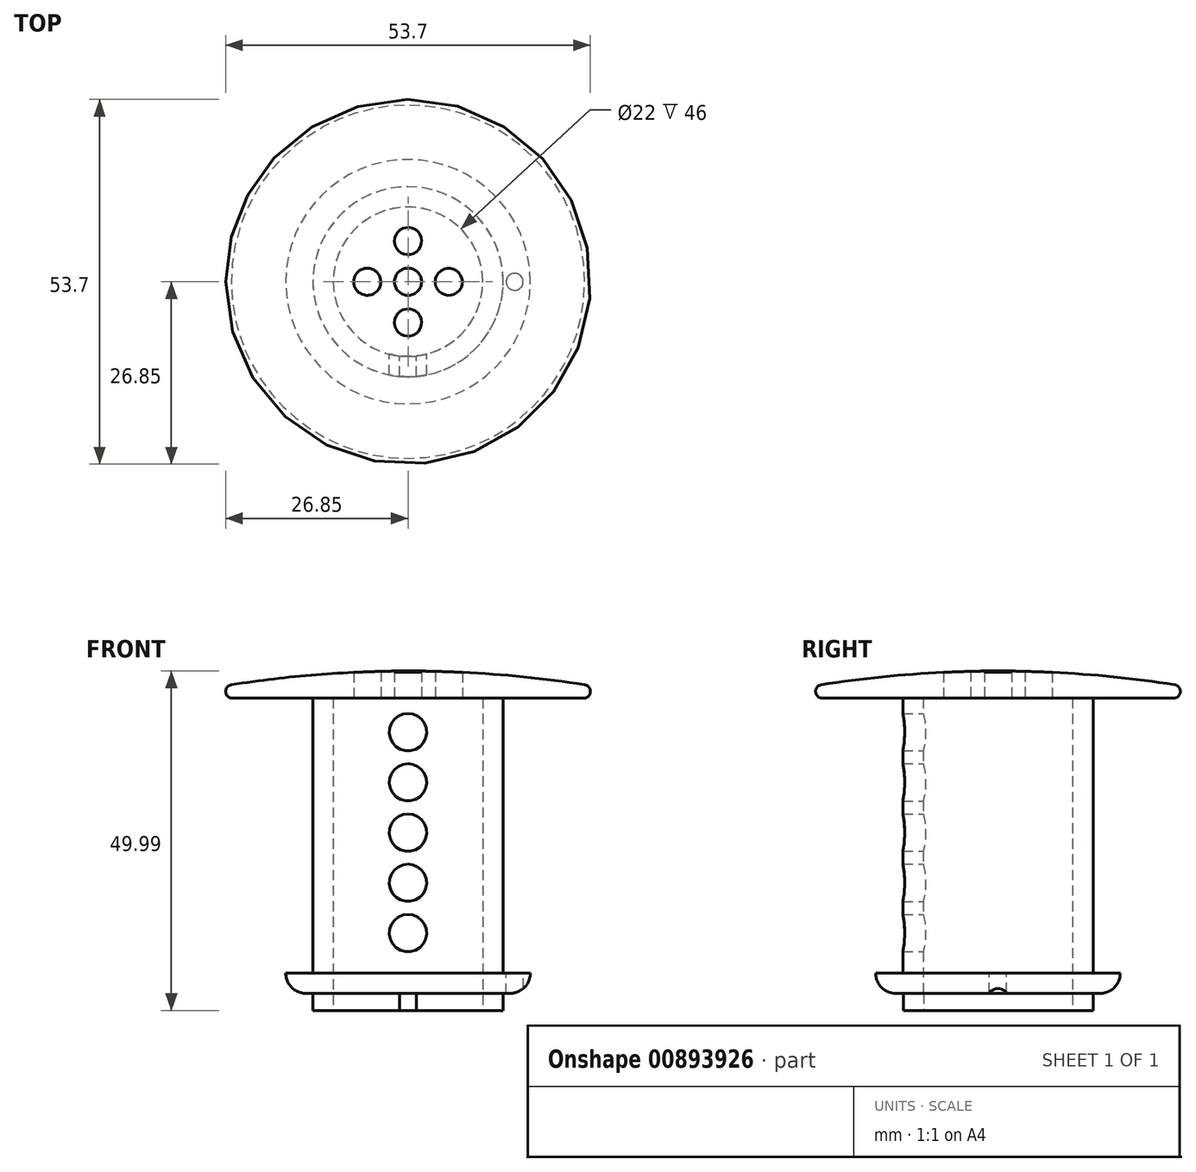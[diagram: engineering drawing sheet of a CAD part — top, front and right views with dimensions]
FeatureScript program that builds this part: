
annotation { "Feature Type Name" : "Feature", "Feature Type Description" : "" }
export const myFeature = defineFeature(function(context is Context, id is Id, definition is map)
    precondition{}
    {
        {
            var Q0;
            Q0=qCreatedBy(makeId("Front.planeOp"),FACE);
            var sketch = newSketch(context, id + "F0", { "sketchPlane" : qUnion([Q0])});
            skArc(sketch, "E0", {"start": v(26, -2.02) * mm, "mid": v(13.04, -0.5) * mm, "end": v(0, 0) * mm});
            skArc(sketch, "E1", {"start": v(26, -4) * mm, "mid": v(26.85, -3.01) * mm, "end": v(26, -2.02) * mm});
            skLineSegment(sketch, "E2", {"start": v(26, -4) * mm, "end": v(14, -4) * mm});
            skLineSegment(sketch, "E3", {"start": v(14, -4) * mm, "end": v(14, -44.5) * mm});
            skLineSegment(sketch, "E4", {"start": v(14, -44.5) * mm, "end": v(18, -44.5) * mm});
            skArc(sketch, "E5", {"start": v(15, -47.5) * mm, "mid": v(17.12, -46.62) * mm, "end": v(18, -44.5) * mm});
            skLineSegment(sketch, "E6", {"start": v(15, -47.5) * mm, "end": v(14, -47.5) * mm});
            skLineSegment(sketch, "E7", {"start": v(14, -47.5) * mm, "end": v(14, -50) * mm});
            skLineSegment(sketch, "E8", {"start": v(14, -50) * mm, "end": v(11, -50) * mm});
            skLineSegment(sketch, "E9", {"start": v(11, -50) * mm, "end": v(11, -4) * mm});
            skLineSegment(sketch, "E10", {"start": v(11, -4) * mm, "end": v(0, -4) * mm});
            skLineSegment(sketch, "E11", {"start": v(0, -4) * mm, "end": v(0, 0) * mm});
            skLineSegment(sketch, "E12", {"start": v(0, -4) * mm, "end": v(0, -44.5) * mm, "construction": true});
            skLineSegment(sketch, "E13", {"start": v(14, -44.5) * mm, "end": v(0, -44.5) * mm, "construction": true});
            skCircle(sketch, "E14", {"center": v(0, -9) * mm, "radius": 2.75 * mm});
            skCircle(sketch, "E15.1.0.0", {"center": v(0, -16.4) * mm, "radius": 2.75 * mm});
            skCircle(sketch, "E15.2.0.0", {"center": v(0, -23.8) * mm, "radius": 2.75 * mm});
            skCircle(sketch, "E15.3.0.0", {"center": v(0, -31.2) * mm, "radius": 2.75 * mm});
            skCircle(sketch, "E15.4.0.0", {"center": v(0, -38.6) * mm, "radius": 2.75 * mm});
            skLineSegment(sketch, "E15.direction1", {"start": v(0, -9) * mm, "end": v(0, -16.4) * mm, "construction": true});
            skLineSegment(sketch, "E16.bottom", {"start": v(-1.25, -47.5) * mm, "end": v(1.25, -47.5) * mm});
            skLineSegment(sketch, "E16.top", {"start": v(-1.25, -50) * mm, "end": v(1.25, -50) * mm});
            skLineSegment(sketch, "E16.left", {"start": v(-1.25, -47.5) * mm, "end": v(-1.25, -50) * mm});
            skLineSegment(sketch, "E16.right", {"start": v(1.25, -47.5) * mm, "end": v(1.25, -50) * mm});
            skLineSegment(sketch, "E17", {"start": v(0, -44.5) * mm, "end": v(0, -47.5) * mm, "construction": true});
            skSolve(sketch);
        }
        {
            var Q0;
            Q0=makeQuery(id+"F0.imprint","IMPRINT",FACE,{"disambiguationData":[TD([[makeQuery(id+"F0.imprint","IMPRINT",EDGE,{"derivedFrom":sQuery(id+"F0.wireOp",EDGE,"E0")}),1.0]])]});
            var Q1;
            Q1=sQuery(id+"F0.wireOp",EDGE,"E11");
            revolve(context, id + "F1", {"surfaceOperationType" : NewSurfaceOperationType.NEW, "entities" : qUnion([Q0]), "axis" : qUnion([Q1]), "revolveType" : RevolveType.FULL});
        }
        {
            var Q0;
            Q0=makeQuery(id+"F1.opRevolve","SWEPT_FACE",FACE,{"disambiguationData":[OSD([sQuery(id+"F0.wireOp",EDGE,"E2")])]});
            var sketch = newSketch(context, id + "F2", { "sketchPlane" : qUnion([Q0])});
            skCircle(sketch, "E18", {"center": v(0, 0) * mm, "radius": 2 * mm});
            skCircle(sketch, "E19", {"center": v(6, 0) * mm, "radius": 2 * mm});
            skCircle(sketch, "E20", {"center": v(0, -6) * mm, "radius": 2 * mm});
            skCircle(sketch, "E21", {"center": v(-6, 0) * mm, "radius": 2 * mm});
            skCircle(sketch, "E22", {"center": v(0, 6) * mm, "radius": 2 * mm});
            skLineSegment(sketch, "E23", {"start": v(0, 0) * mm, "end": v(-6, 0) * mm, "construction": true});
            skLineSegment(sketch, "E24", {"start": v(0, 0) * mm, "end": v(0, -6) * mm, "construction": true});
            skLineSegment(sketch, "E25", {"start": v(0, 0) * mm, "end": v(6, 0) * mm, "construction": true});
            skLineSegment(sketch, "E26", {"start": v(0, 0) * mm, "end": v(0, 6) * mm, "construction": true});
            skCircle(sketch, "E27.0.0", {"center": v(0, 0) * mm, "radius": 18 * mm});
            skCircle(sketch, "E28", {"center": v(15.7, 0) * mm, "radius": 1.25 * mm});
            skCircle(sketch, "E29.0", {"center": v(0, 0) * mm, "radius": 14 * mm});
            skLineSegment(sketch, "E30", {"start": v(18, 0) * mm, "end": v(14, 0) * mm, "construction": true});
            skSolve(sketch);
        }
        {
            var Q0;
            Q0=makeQuery(id+"F2.imprint","IMPRINT",FACE,{"disambiguationData":[TD([[makeQuery(id+"F2.imprint","IMPRINT",EDGE,{"derivedFrom":sQuery(id+"F2.wireOp",EDGE,"E21")}),1.0]])]});
            var Q1;
            Q1=makeQuery(id+"F2.imprint","IMPRINT",FACE,{"disambiguationData":[TD([[makeQuery(id+"F2.imprint","IMPRINT",EDGE,{"derivedFrom":sQuery(id+"F2.wireOp",EDGE,"E18")}),1.0]])]});
            var Q2;
            Q2=makeQuery(id+"F2.imprint","IMPRINT",FACE,{"disambiguationData":[TD([[makeQuery(id+"F2.imprint","IMPRINT",EDGE,{"derivedFrom":sQuery(id+"F2.wireOp",EDGE,"E20")}),1.0]])]});
            var Q3;
            Q3=makeQuery(id+"F2.imprint","IMPRINT",FACE,{"disambiguationData":[TD([[makeQuery(id+"F2.imprint","IMPRINT",EDGE,{"derivedFrom":sQuery(id+"F2.wireOp",EDGE,"E19")}),1.0]])]});
            var Q4;
            Q4=makeQuery(id+"F2.imprint","IMPRINT",FACE,{"disambiguationData":[TD([[makeQuery(id+"F2.imprint","IMPRINT",EDGE,{"derivedFrom":sQuery(id+"F2.wireOp",EDGE,"E22")}),1.0]])]});
            extrude(context, id + "F3", {"entities" : qUnion([Q0, Q1, Q2, Q3, Q4]), "operationType" : NewBodyOperationType.REMOVE, "endBound" : BoundingType.THROUGH_ALL, "oppositeDirection" : true, "depth" : 25 * mm, "offsetDistance" : 25 * mm});
        }
        {
            var Q0;
            Q0=makeQuery(id+"F2.imprint","IMPRINT",FACE,{"disambiguationData":[TD([[makeQuery(id+"F2.imprint","IMPRINT",EDGE,{"derivedFrom":sQuery(id+"F2.wireOp",EDGE,"E28")}),1.0]])]});
            extrude(context, id + "F4", {"entities" : qUnion([Q0]), "operationType" : NewBodyOperationType.REMOVE, "endBound" : BoundingType.THROUGH_ALL, "depth" : 25 * mm, "offsetDistance" : 25 * mm});
        }
        {
            var Q0;
            Q0=makeQuery(id+"F0.imprint","IMPRINT",FACE,{"disambiguationData":[TD([[makeQuery(id+"F0.imprint","IMPRINT",EDGE,{"derivedFrom":sQuery(id+"F0.wireOp",EDGE,"E14")}),1.0]])]});
            var Q1;
            Q1=makeQuery(id+"F0.imprint","IMPRINT",FACE,{"disambiguationData":[TD([[makeQuery(id+"F0.imprint","IMPRINT",EDGE,{"derivedFrom":sQuery(id+"F0.wireOp",EDGE,"E15.1.0.0")}),1.0]])]});
            var Q2;
            Q2=makeQuery(id+"F0.imprint","IMPRINT",FACE,{"disambiguationData":[TD([[makeQuery(id+"F0.imprint","IMPRINT",EDGE,{"derivedFrom":sQuery(id+"F0.wireOp",EDGE,"E15.2.0.0")}),1.0]])]});
            var Q3;
            Q3=makeQuery(id+"F0.imprint","IMPRINT",FACE,{"disambiguationData":[TD([[makeQuery(id+"F0.imprint","IMPRINT",EDGE,{"derivedFrom":sQuery(id+"F0.wireOp",EDGE,"E15.3.0.0")}),1.0]])]});
            var Q4;
            Q4=makeQuery(id+"F0.imprint","IMPRINT",FACE,{"disambiguationData":[TD([[makeQuery(id+"F0.imprint","IMPRINT",EDGE,{"derivedFrom":sQuery(id+"F0.wireOp",EDGE,"E15.4.0.0")}),1.0]])]});
            var Q5;
            Q5=sQuery(id+"F0.wireOp",EDGE,"E14");
            var Q6;
            Q6=sQuery(id+"F0.wireOp",EDGE,"E15.1.0.0");
            var Q7;
            Q7=sQuery(id+"F0.wireOp",EDGE,"E15.2.0.0");
            var Q8;
            Q8=sQuery(id+"F0.wireOp",EDGE,"E15.3.0.0");
            var Q9;
            Q9=sQuery(id+"F0.wireOp",EDGE,"E15.4.0.0");
            extrude(context, id + "F5", {"entities" : qUnion([Q0, Q1, Q2, Q3, Q4]), "operationType" : NewBodyOperationType.REMOVE, "surfaceEntities" : qUnion([Q5, Q6, Q7, Q8, Q9]), "endBound" : BoundingType.THROUGH_ALL, "depth" : 25 * mm, "offsetDistance" : 25 * mm});
        }
        {
            var Q0;
            Q0=makeQuery(id+"F0.imprint","IMPRINT",FACE,{"disambiguationData":[TD([[makeQuery(id+"F0.imprint","IMPRINT",EDGE,{"derivedFrom":sQuery(id+"F0.wireOp",EDGE,"E16.bottom")}),-1.0]])]});
            extrude(context, id + "F6", {"entities" : qUnion([Q0]), "operationType" : NewBodyOperationType.REMOVE, "endBound" : BoundingType.THROUGH_ALL, "depth" : 25 * mm, "offsetDistance" : 25 * mm});
        }
    });
